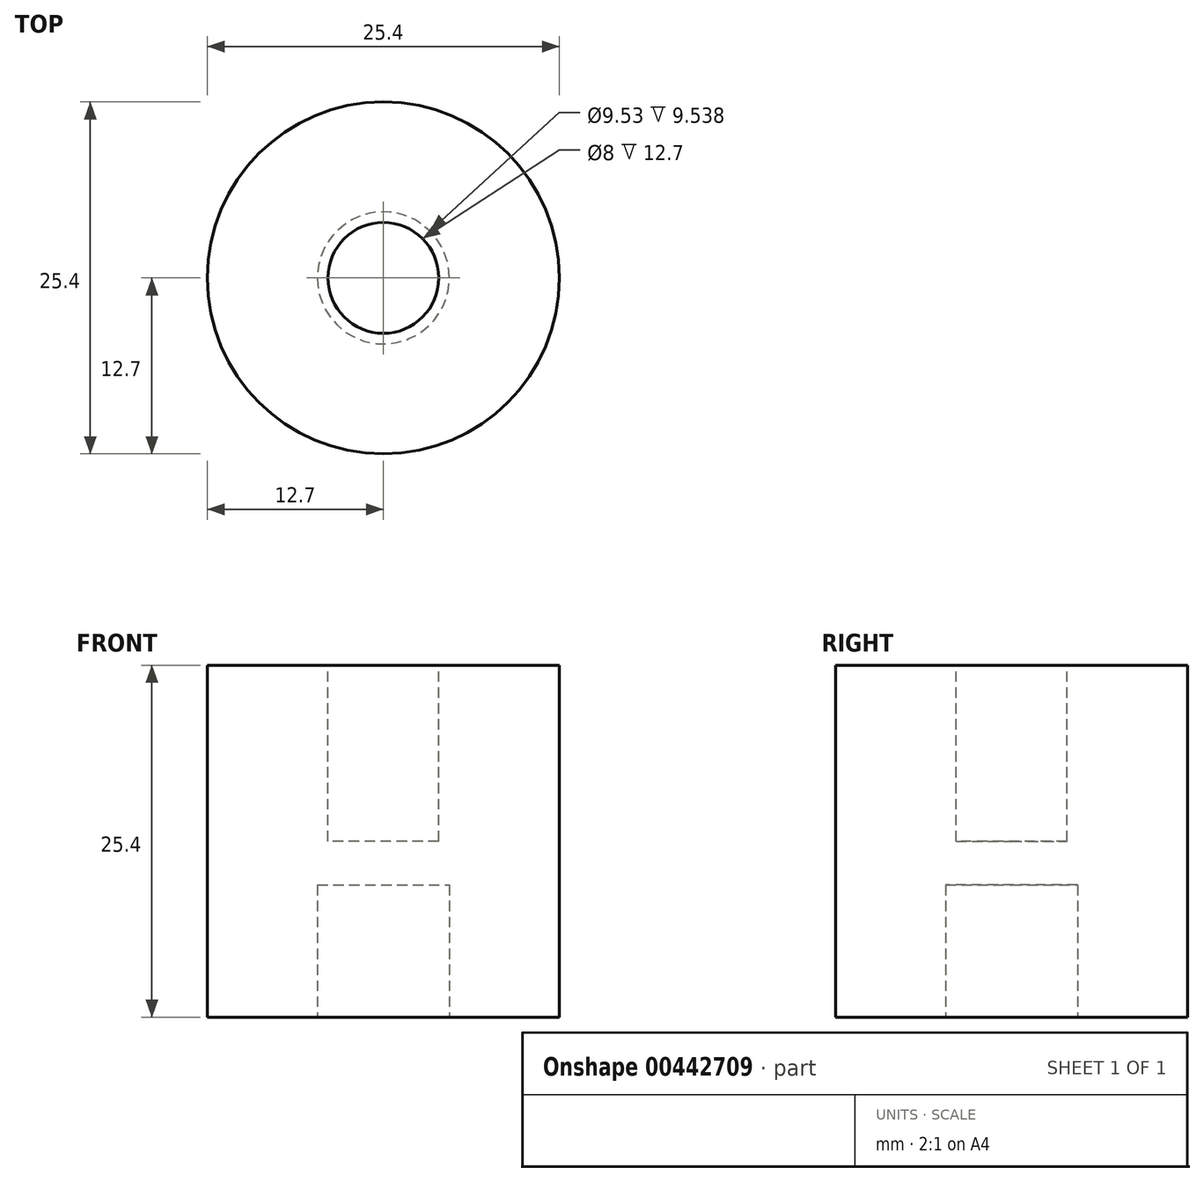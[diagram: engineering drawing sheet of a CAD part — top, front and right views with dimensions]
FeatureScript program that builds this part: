
annotation { "Feature Type Name" : "Feature", "Feature Type Description" : "" }
export const myFeature = defineFeature(function(context is Context, id is Id, definition is map)
    precondition{}
    {
        {
            var Q0;
            Q0=qCreatedBy(makeId("Top.planeOp"),FACE);
            var sketch = newSketch(context, id + "F0", { "sketchPlane" : qUnion([Q0])});
            skCircle(sketch, "E0", {"center": v(0, 0) * mm, "radius": 12.7 * mm});
            skSolve(sketch);
        }
        {
            var Q0;
            Q0=makeQuery(id+"F0.imprint","IMPRINT",FACE,{"disambiguationData":[TD([[makeQuery(id+"F0.imprint","IMPRINT",EDGE,{"derivedFrom":sQuery(id+"F0.wireOp",EDGE,"E0")}),1.0]])]});
            extrude(context, id + "F1", {"entities" : qUnion([Q0]), "depth" : 25.4 * mm});
        }
        {
            var Q0;
            Q0=makeQuery(id+"F1.opExtrude","CAP_FACE",FACE,{"disambiguationData":[OSD([sQuery(id+"F0.wireOp",EDGE,"E0")])],"isStart":false});
            var sketch = newSketch(context, id + "F2", { "sketchPlane" : qUnion([Q0])});
            skCircle(sketch, "E1", {"center": v(0, 0) * mm, "radius": 4 * mm});
            skSolve(sketch);
        }
        {
            var Q0;
            Q0=makeQuery(id+"F1.opExtrude","CAP_FACE",FACE,{"disambiguationData":[OSD([sQuery(id+"F0.wireOp",EDGE,"E0")])],"isStart":true});
            var sketch = newSketch(context, id + "F3", { "sketchPlane" : qUnion([Q0])});
            skCircle(sketch, "E2", {"center": v(0, 0) * mm, "radius": 4.76 * mm});
            skSolve(sketch);
        }
        {
            var Q0;
            Q0=makeQuery(id+"F3.imprint","IMPRINT",FACE,{"disambiguationData":[TD([[makeQuery(id+"F3.imprint","IMPRINT",EDGE,{"derivedFrom":sQuery(id+"F3.wireOp",EDGE,"E2")}),1.0]])]});
            extrude(context, id + "F4", {"entities" : qUnion([Q0]), "operationType" : NewBodyOperationType.REMOVE, "oppositeDirection" : true, "depth" : 9.54 * mm});
        }
        {
            var Q0;
            Q0=makeQuery(id+"F2.imprint","IMPRINT",FACE,{"disambiguationData":[TD([[makeQuery(id+"F2.imprint","IMPRINT",EDGE,{"derivedFrom":sQuery(id+"F2.wireOp",EDGE,"E1")}),1.0]])]});
            extrude(context, id + "F5", {"entities" : qUnion([Q0]), "operationType" : NewBodyOperationType.REMOVE, "oppositeDirection" : true, "depth" : 12.7 * mm});
        }
    });
